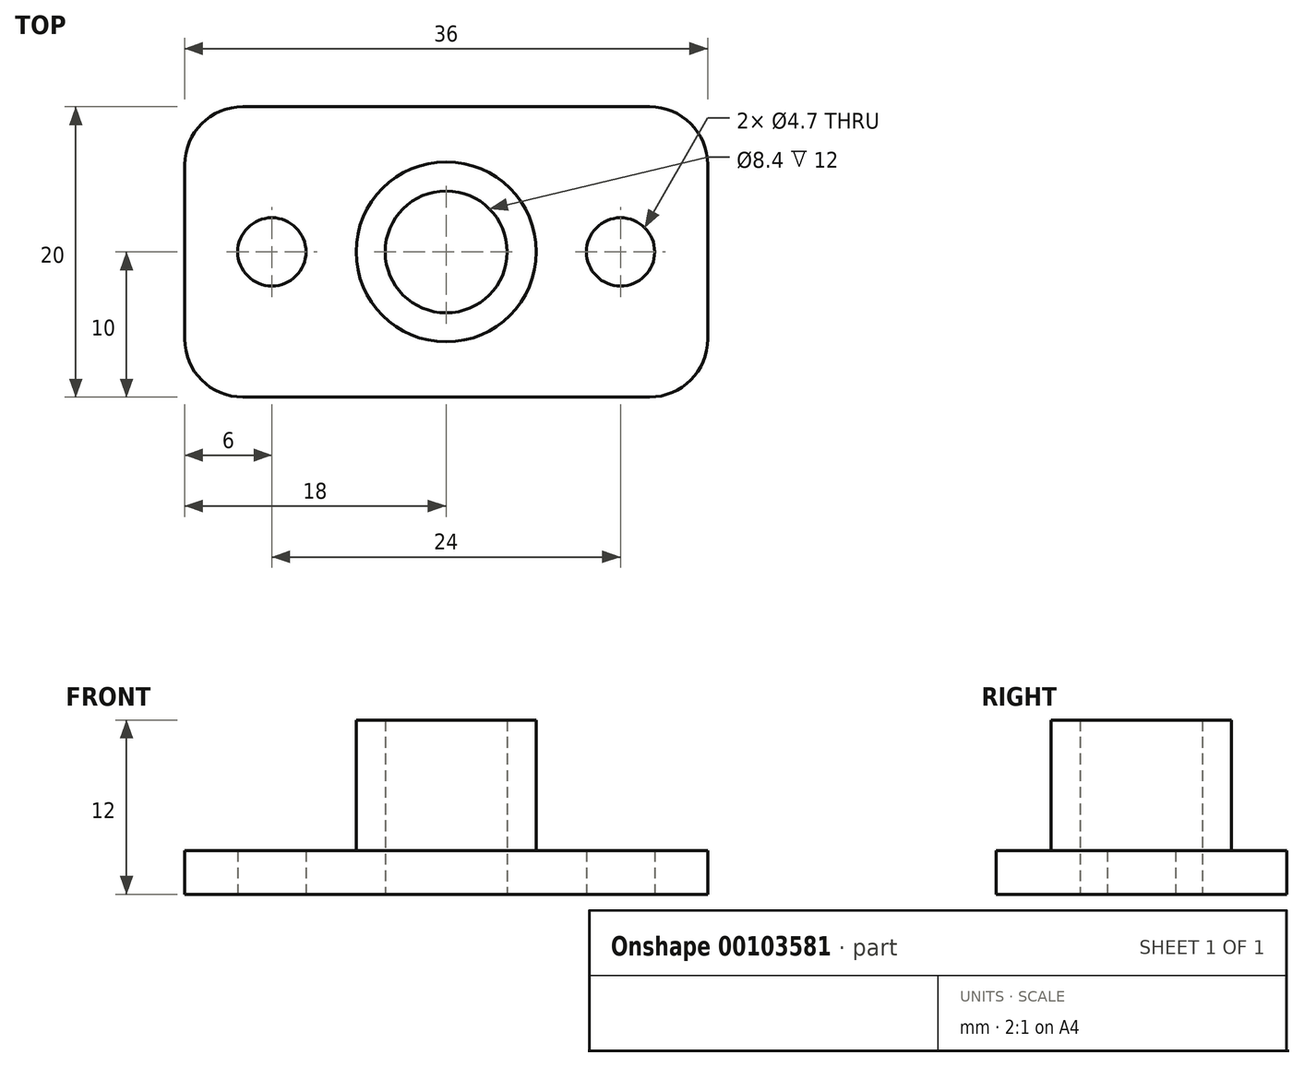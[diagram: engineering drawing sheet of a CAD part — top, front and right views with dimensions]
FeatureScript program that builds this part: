
annotation { "Feature Type Name" : "Feature", "Feature Type Description" : "" }
export const myFeature = defineFeature(function(context is Context, id is Id, definition is map)
    precondition{}
    {
        {
            var Q0;
            Q0=qCreatedBy(makeId("Top.planeOp"),FACE);
            var sketch = newSketch(context, id + "F0", { "sketchPlane" : qUnion([Q0])});
            skLineSegment(sketch, "E0.bottom", {"start": v(18, -10) * mm, "end": v(-18, -10) * mm});
            skLineSegment(sketch, "E0.top", {"start": v(18, 10) * mm, "end": v(-18, 10) * mm});
            skLineSegment(sketch, "E0.left", {"start": v(18, -10) * mm, "end": v(18, 10) * mm});
            skLineSegment(sketch, "E0.right", {"start": v(-18, -10) * mm, "end": v(-18, 10) * mm});
            skPoint(sketch, "E0.middle", {"position": v(0, 0) * mm});
            skCircle(sketch, "E1", {"center": v(0, 0) * mm, "radius": 4.2 * mm});
            skCircle(sketch, "E2.0", {"center": v(0, 0) * mm, "radius": 6.2 * mm});
            skLineSegment(sketch, "E3", {"start": v(-18, 0) * mm, "end": v(18, 0) * mm, "construction": true});
            skCircle(sketch, "E4", {"center": v(-12, 0) * mm, "radius": 2.35 * mm});
            skCircle(sketch, "E5", {"center": v(12, 0) * mm, "radius": 2.35 * mm});
            skSolve(sketch);
        }
        {
            var Q0;
            Q0=makeQuery(id+"F0.imprint","IMPRINT",FACE,{"disambiguationData":[TD([[makeQuery(id+"F0.imprint","IMPRINT",EDGE,{"derivedFrom":sQuery(id+"F0.wireOp",EDGE,"E0.bottom")}),-1.0]])]});
            extrude(context, id + "F1", {"entities" : qUnion([Q0]), "depth" : 3 * mm});
        }
        {
            var Q0;
            Q0=makeQuery(id+"F0.imprint","IMPRINT",FACE,{"disambiguationData":[TD([[makeQuery(id+"F0.imprint","IMPRINT",EDGE,{"derivedFrom":sQuery(id+"F0.wireOp",EDGE,"E1")}),-1.0]])]});
            extrude(context, id + "F2", {"entities" : qUnion([Q0]), "operationType" : NewBodyOperationType.ADD, "depth" : 12 * mm});
        }
        {
            var Q0;
            Q0=makeQuery(id+"F1.opExtrude","SWEPT_EDGE",EDGE,{"disambiguationData":[OSD([sQuery(id+"F0.wireOp",EDGE,"E0.top"),sQuery(id+"F0.wireOp",EDGE,"E0.right")])]});
            var Q1;
            Q1=makeQuery(id+"F1.opExtrude","SWEPT_EDGE",EDGE,{"disambiguationData":[OSD([sQuery(id+"F0.wireOp",EDGE,"E0.bottom"),sQuery(id+"F0.wireOp",EDGE,"E0.right")])]});
            var Q2;
            Q2=makeQuery(id+"F1.opExtrude","SWEPT_EDGE",EDGE,{"disambiguationData":[OSD([sQuery(id+"F0.wireOp",EDGE,"E0.bottom"),sQuery(id+"F0.wireOp",EDGE,"E0.left")])]});
            var Q3;
            Q3=makeQuery(id+"F1.opExtrude","SWEPT_EDGE",EDGE,{"disambiguationData":[OSD([sQuery(id+"F0.wireOp",EDGE,"E0.top"),sQuery(id+"F0.wireOp",EDGE,"E0.left")])]});
            fillet(context, id + "F3", {"entities" : qUnion([Q0, Q1, Q2, Q3]), "radius" : 4 * mm, "tangentPropagation" : true, "allowEdgeOverflow" : false});
        }
    });
